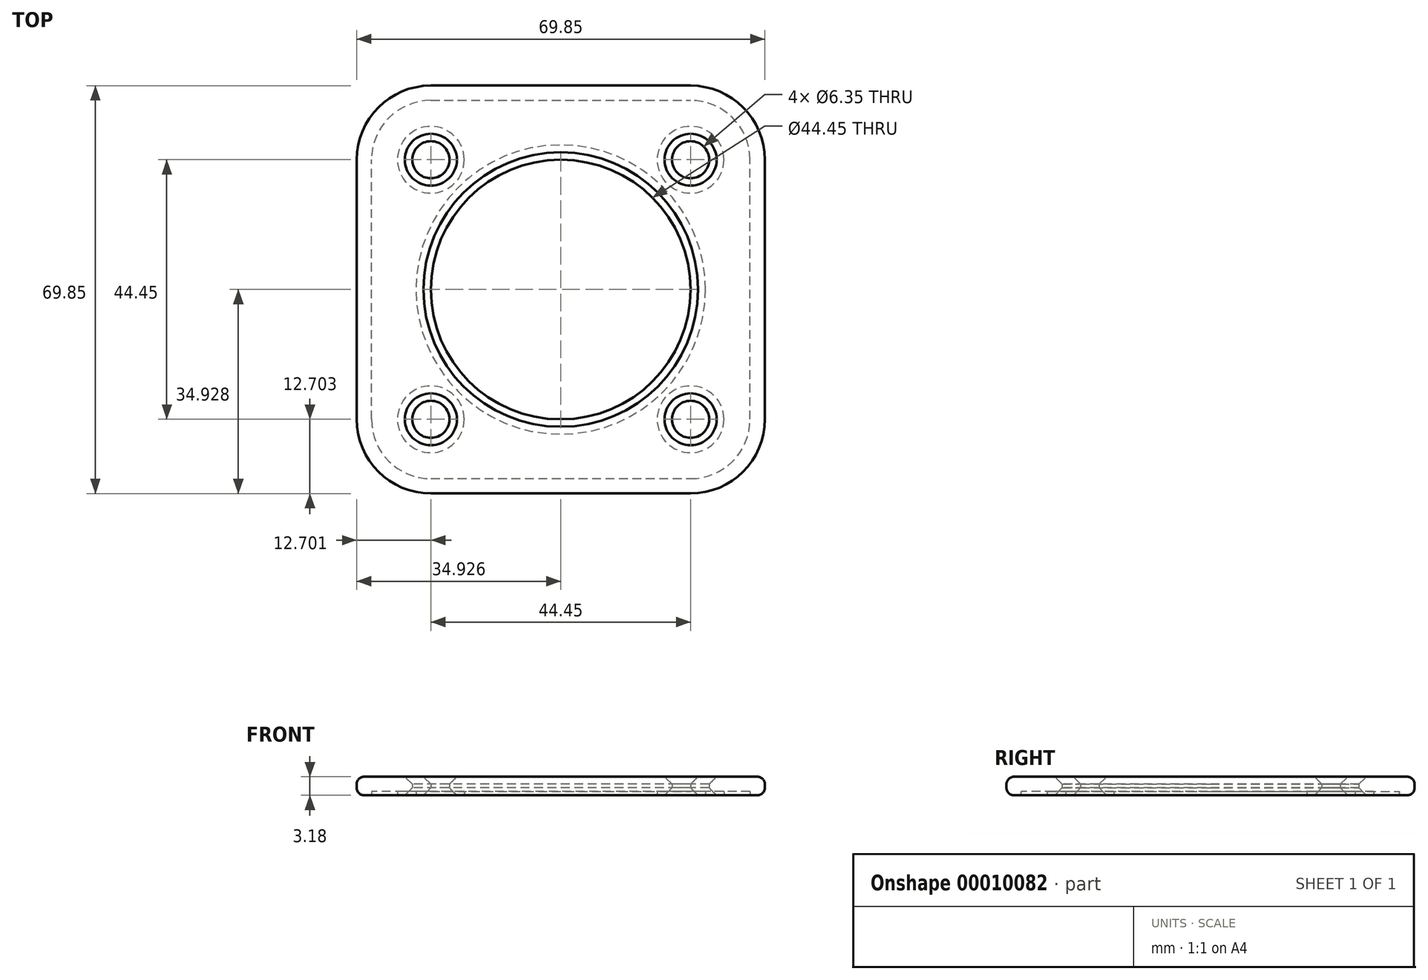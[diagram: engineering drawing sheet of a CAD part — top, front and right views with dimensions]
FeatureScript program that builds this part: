
annotation { "Feature Type Name" : "Feature", "Feature Type Description" : "" }
export const myFeature = defineFeature(function(context is Context, id is Id, definition is map)
    precondition{}
    {
        {
            var Q0;
            Q0=qCreatedBy(makeId("Top.planeOp"),FACE);
            var sketch = newSketch(context, id + "F0", { "sketchPlane" : qUnion([Q0])});
            skLineSegment(sketch, "E0.bottom", {"start": v(-35.17, 52.36) * mm, "end": v(9.28, 52.36) * mm});
            skLineSegment(sketch, "E0.top", {"start": v(-35.17, -17.49) * mm, "end": v(9.28, -17.49) * mm});
            skLineSegment(sketch, "E0.left", {"start": v(-47.87, 39.66) * mm, "end": v(-47.87, -4.79) * mm});
            skLineSegment(sketch, "E0.right", {"start": v(21.98, 39.66) * mm, "end": v(21.98, -4.79) * mm});
            skPoint(sketch, "E1.visualSharp", {"position": v(-47.87, 52.36) * mm});
            skArc(sketch, "E1.filletArc", {"start": v(-35.17, 52.36) * mm, "mid": v(-44.15, 48.64) * mm, "end": v(-47.87, 39.66) * mm});
            skPoint(sketch, "E2.visualSharp", {"position": v(21.98, 52.36) * mm});
            skArc(sketch, "E2.filletArc", {"start": v(21.98, 39.66) * mm, "mid": v(18.26, 48.64) * mm, "end": v(9.28, 52.36) * mm});
            skPoint(sketch, "E3.visualSharp", {"position": v(21.98, -17.49) * mm});
            skArc(sketch, "E3.filletArc", {"start": v(9.28, -17.49) * mm, "mid": v(18.26, -13.77) * mm, "end": v(21.98, -4.79) * mm});
            skPoint(sketch, "E4.visualSharp", {"position": v(-47.87, -17.49) * mm});
            skArc(sketch, "E4.filletArc", {"start": v(-47.87, -4.79) * mm, "mid": v(-44.15, -13.77) * mm, "end": v(-35.17, -17.49) * mm});
            skCircle(sketch, "E5", {"center": v(-12.94, 17.44) * mm, "radius": 22.23 * mm});
            skCircle(sketch, "E6", {"center": v(-35.17, 39.66) * mm, "radius": 3.18 * mm});
            skCircle(sketch, "E7.0.1.0", {"center": v(-35.17, -4.79) * mm, "radius": 3.18 * mm});
            skCircle(sketch, "E7.1.0.0", {"center": v(9.28, 39.66) * mm, "radius": 3.18 * mm});
            skCircle(sketch, "E7.1.1.0", {"center": v(9.28, -4.79) * mm, "radius": 3.18 * mm});
            skLineSegment(sketch, "E7.direction1", {"start": v(-35.17, 39.66) * mm, "end": v(9.28, 39.66) * mm, "construction": true});
            skLineSegment(sketch, "E7.direction2", {"start": v(-35.17, 39.66) * mm, "end": v(-35.17, -4.79) * mm, "construction": true});
            skSolve(sketch);
        }
        {
            var Q0;
            Q0=makeQuery(id+"F0.imprint","IMPRINT",FACE,{"disambiguationData":[TD([[makeQuery(id+"F0.imprint","IMPRINT",EDGE,{"derivedFrom":sQuery(id+"F0.wireOp",EDGE,"E0.bottom")}),-1.0]])]});
            extrude(context, id + "F1", {"entities" : qUnion([Q0]), "depth" : 3.17 * mm});
        }
        {
            var Q0;
            Q0=makeQuery(id+"F1.opExtrude","CAP_EDGE",EDGE,{"disambiguationData":[OSD([sQuery(id+"F0.wireOp",EDGE,"E0.top")])],"isStart":false});
            var Q1;
            Q1=makeQuery(id+"F1.opExtrude","CAP_EDGE",EDGE,{"disambiguationData":[OSD([sQuery(id+"F0.wireOp",EDGE,"E0.top")])],"isStart":true});
            fillet(context, id + "F2", {"entities" : qUnion([Q0, Q1]), "radius" : 1.27 * mm, "tangentPropagation" : true, "allowEdgeOverflow" : false});
        }
        {
            var Q0;
            Q0=makeQuery(id+"F1.opExtrude","CAP_FACE",FACE,{"disambiguationData":[OSD([sQuery(id+"F0.wireOp",EDGE,"E0.bottom"),sQuery(id+"F0.wireOp",EDGE,"E0.top"),sQuery(id+"F0.wireOp",EDGE,"E0.left"),sQuery(id+"F0.wireOp",EDGE,"E0.right"),sQuery(id+"F0.wireOp",EDGE,"E1.filletArc"),sQuery(id+"F0.wireOp",EDGE,"E2.filletArc"),sQuery(id+"F0.wireOp",EDGE,"E3.filletArc"),sQuery(id+"F0.wireOp",EDGE,"E4.filletArc"),sQuery(id+"F0.wireOp",EDGE,"E5"),sQuery(id+"F0.wireOp",EDGE,"E6"),sQuery(id+"F0.wireOp",EDGE,"E7.0.1.0"),sQuery(id+"F0.wireOp",EDGE,"E7.1.0.0"),sQuery(id+"F0.wireOp",EDGE,"E7.1.1.0")])],"isStart":true});
            shell(context, id + "F3", {"entities" : qUnion([Q0]), "thickness" : 2.54 * mm});
        }
        {
            var Q0;
            Q0=makeQuery(id+"F1.opExtrude","CAP_EDGE",EDGE,{"disambiguationData":[OSD([sQuery(id+"F0.wireOp",EDGE,"E7.0.1.0")])],"isStart":false});
            var Q1;
            Q1=makeQuery(id+"F1.opExtrude","CAP_EDGE",EDGE,{"disambiguationData":[OSD([sQuery(id+"F0.wireOp",EDGE,"E6")])],"isStart":false});
            var Q2;
            Q2=makeQuery(id+"F1.opExtrude","CAP_EDGE",EDGE,{"disambiguationData":[OSD([sQuery(id+"F0.wireOp",EDGE,"E7.1.0.0")])],"isStart":false});
            var Q3;
            Q3=makeQuery(id+"F1.opExtrude","CAP_EDGE",EDGE,{"disambiguationData":[OSD([sQuery(id+"F0.wireOp",EDGE,"E7.1.1.0")])],"isStart":false});
            var Q4;
            Q4=makeQuery(id+"F1.opExtrude","CAP_EDGE",EDGE,{"disambiguationData":[OSD([sQuery(id+"F0.wireOp",EDGE,"E7.1.0.0")])],"isStart":true});
            var Q5;
            Q5=makeQuery(id+"F1.opExtrude","CAP_EDGE",EDGE,{"disambiguationData":[OSD([sQuery(id+"F0.wireOp",EDGE,"E6")])],"isStart":true});
            var Q6;
            Q6=makeQuery(id+"F1.opExtrude","CAP_EDGE",EDGE,{"disambiguationData":[OSD([sQuery(id+"F0.wireOp",EDGE,"E7.0.1.0")])],"isStart":true});
            var Q7;
            Q7=makeQuery(id+"F1.opExtrude","CAP_EDGE",EDGE,{"disambiguationData":[OSD([sQuery(id+"F0.wireOp",EDGE,"E7.1.1.0")])],"isStart":true});
            chamfer(context, id + "F4", {"entities" : qUnion([Q0, Q1, Q2, Q3, Q4, Q5, Q6, Q7]), "width" : 1.27 * mm, "tangentPropagation" : true});
        }
        {
            var Q0;
            Q0=makeQuery(id+"F1.opExtrude","CAP_EDGE",EDGE,{"disambiguationData":[OSD([sQuery(id+"F0.wireOp",EDGE,"E5")])],"isStart":false});
            var Q1;
            Q1=makeQuery(id+"F1.opExtrude","CAP_EDGE",EDGE,{"disambiguationData":[OSD([sQuery(id+"F0.wireOp",EDGE,"E5")])],"isStart":true});
            chamfer(context, id + "F5", {"entities" : qUnion([Q0, Q1]), "width" : 1.27 * mm, "tangentPropagation" : true});
        }
    });
